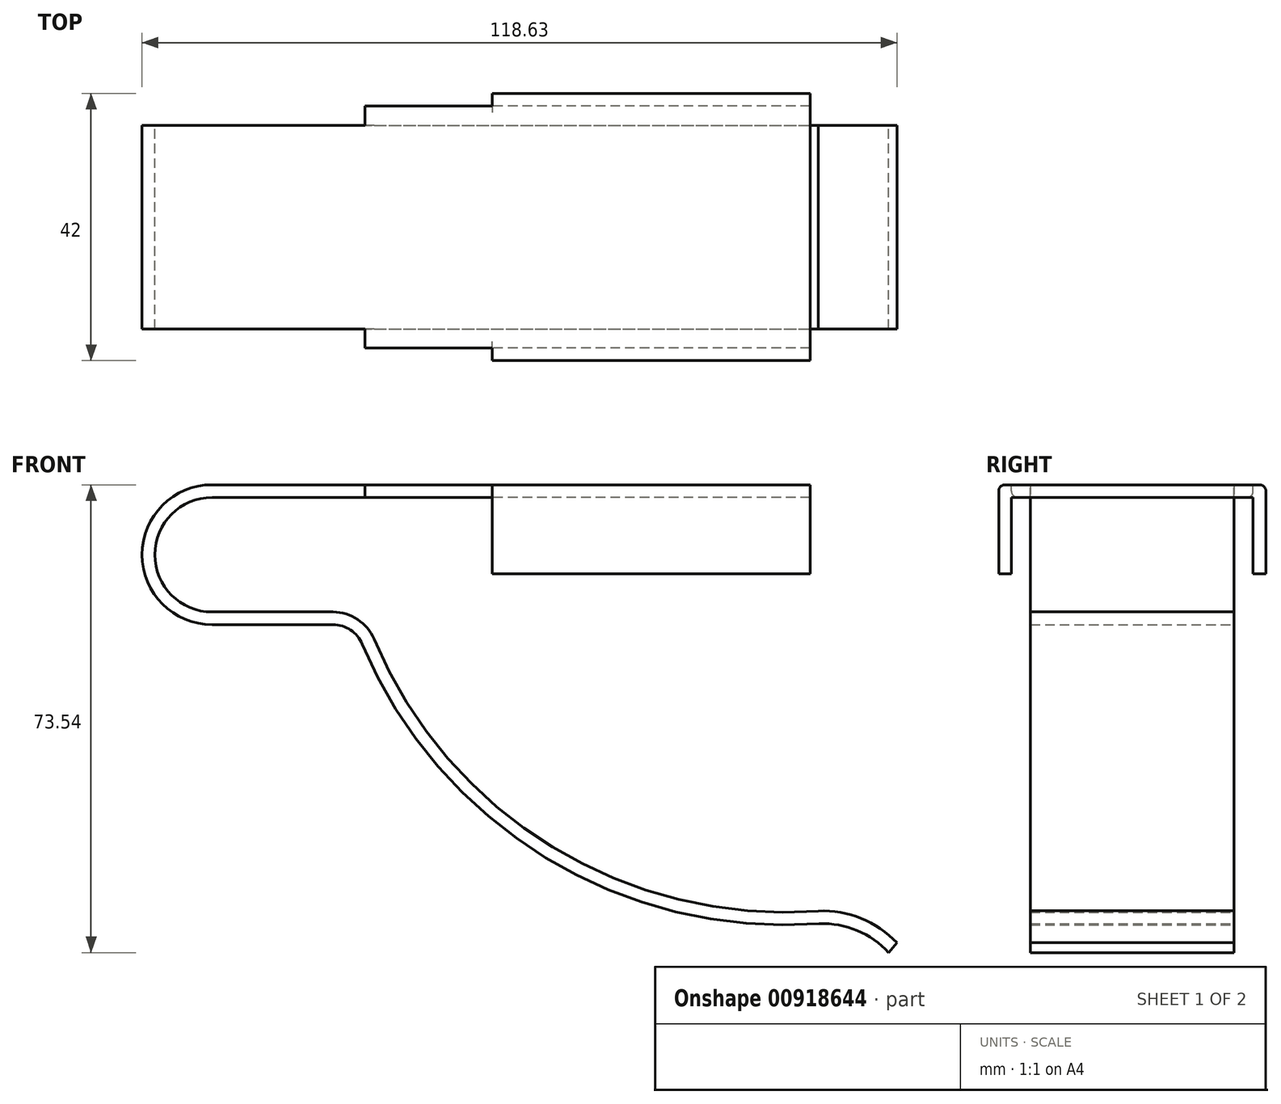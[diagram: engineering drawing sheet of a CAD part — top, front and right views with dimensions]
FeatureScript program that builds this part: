
annotation { "Feature Type Name" : "Feature", "Feature Type Description" : "" }
export const myFeature = defineFeature(function(context is Context, id is Id, definition is map)
    precondition{}
    {
        {
            var Q0;
            Q0=qCreatedBy(makeId("Front.planeOp"),FACE);
            var sketch = newSketch(context, id + "F0", { "sketchPlane" : qUnion([Q0])});
            skArc(sketch, "E0", {"start": v(0, 11) * mm, "mid": v(-11, 0) * mm, "end": v(0, -11) * mm});
            skLineSegment(sketch, "E1", {"start": v(0, 11) * mm, "end": v(94, 11) * mm});
            skLineSegment(sketch, "E2", {"start": v(0, -11) * mm, "end": v(19, -11) * mm});
            skArc(sketch, "E3", {"start": v(23.61, -14.06) * mm, "mid": v(52.42, -47.62) * mm, "end": v(95.41, -58) * mm});
            skArc(sketch, "E4", {"start": v(106.34, -62.54) * mm, "mid": v(101.38, -59.06) * mm, "end": v(95.41, -58) * mm});
            skPoint(sketch, "E5.visualSharp", {"position": v(22.4, -11) * mm});
            skArc(sketch, "E5.filletArc", {"start": v(23.61, -14.06) * mm, "mid": v(21.77, -11.84) * mm, "end": v(19, -11) * mm});
            skArc(sketch, "E6.0", {"start": v(107.63, -61) * mm, "mid": v(102, -57.16) * mm, "end": v(95.3, -56) * mm});
            skArc(sketch, "E6.1", {"start": v(25.45, -13.3) * mm, "mid": v(53.48, -45.92) * mm, "end": v(95.3, -56) * mm});
            skLineSegment(sketch, "E6.2", {"start": v(0, 9) * mm, "end": v(94, 9) * mm});
            skArc(sketch, "E6.3", {"start": v(0, 9) * mm, "mid": v(-9, 0) * mm, "end": v(0, -9) * mm});
            skLineSegment(sketch, "E6.4", {"start": v(0, -9) * mm, "end": v(19, -9) * mm});
            skArc(sketch, "E6.5", {"start": v(25.45, -13.3) * mm, "mid": v(22.88, -10.17) * mm, "end": v(19, -9) * mm});
            skLineSegment(sketch, "E7", {"start": v(94, 11) * mm, "end": v(94, 9) * mm});
            skLineSegment(sketch, "E8", {"start": v(106.34, -62.54) * mm, "end": v(107.63, -61) * mm});
            skSolve(sketch);
        }
        {
            var Q0;
            Q0=qSketchRegion(id+"F0",true);
            extrude(context, id + "F1", {"entities" : qUnion([Q0]), "depth" : 16 * mm, "offsetDistance" : 25 * mm});
        }
        {
            var Q0;
            Q0=makeQuery(id+"F1.opExtrude","SWEPT_FACE",FACE,{"disambiguationData":[OSD([sQuery(id+"F0.wireOp",EDGE,"E1")])]});
            var sketch = newSketch(context, id + "F2", { "sketchPlane" : qUnion([Q0])});
            skLineSegment(sketch, "E9.bottom", {"start": v(94, -16) * mm, "end": v(24, -16) * mm});
            skLineSegment(sketch, "E9.top", {"start": v(94, -19) * mm, "end": v(24, -19) * mm});
            skLineSegment(sketch, "E9.left", {"start": v(94, -16) * mm, "end": v(94, -19) * mm});
            skLineSegment(sketch, "E9.right", {"start": v(24, -16) * mm, "end": v(24, -19) * mm});
            skSolve(sketch);
        }
        {
            var Q0;
            Q0=makeQuery(id+"F2.imprint","IMPRINT",FACE,{"disambiguationData":[TD([[makeQuery(id+"F2.imprint","IMPRINT",EDGE,{"derivedFrom":sQuery(id+"F2.wireOp",EDGE,"E9.bottom")}),-1.0]])]});
            extrude(context, id + "F3", {"entities" : qUnion([Q0]), "operationType" : NewBodyOperationType.ADD, "oppositeDirection" : true, "depth" : 2 * mm, "offsetDistance" : 25 * mm});
        }
        {
            var Q0;
            Q0=makeQuery(id+"F3.opExtrude","SWEPT_FACE",FACE,{"disambiguationData":[OSD([sQuery(id+"F2.wireOp",EDGE,"E9.top")])]});
            var sketch = newSketch(context, id + "F4", { "sketchPlane" : qUnion([Q0])});
            skLineSegment(sketch, "E10.bottom", {"start": v(94, 11) * mm, "end": v(44, 11) * mm});
            skLineSegment(sketch, "E10.top", {"start": v(94, -3) * mm, "end": v(44, -3) * mm});
            skLineSegment(sketch, "E10.left", {"start": v(94, 11) * mm, "end": v(94, -3) * mm});
            skLineSegment(sketch, "E10.right", {"start": v(44, 11) * mm, "end": v(44, -3) * mm});
            skSolve(sketch);
        }
        {
            var Q0;
            Q0=qSketchRegion(id+"F4",true);
            extrude(context, id + "F5", {"entities" : qUnion([Q0]), "operationType" : NewBodyOperationType.ADD, "depth" : 2 * mm, "offsetDistance" : 25 * mm});
        }
        {
            var Q0;
            Q0=makeQuery(id+"F5.opExtrude","CAP_EDGE",EDGE,{"disambiguationData":[OSD([sQuery(id+"F4.wireOp",EDGE,"E10.bottom")])],"isStart":false});
            var Q1;
            {var subQ0=sQuery(id+"F2.wireOp",EDGE,"E9.top");Q1=makeQuery(id+"F5.boolean.opBoolean","SPLIT",EDGE,{"disambiguationData":[topologyDisambiguationEdgeConnected([makeQuery(id+"F5.opExtrude","CAP_FACE",FACE,{"disambiguationData":[OSD([sQuery(id+"F4.wireOp",EDGE,"E10.bottom"),sQuery(id+"F4.wireOp",EDGE,"E10.top"),sQuery(id+"F4.wireOp",EDGE,"E10.left"),sQuery(id+"F4.wireOp",EDGE,"E10.right")])],"isStart":true})])],"derivedFrom":makeQuery(id+"F3.opExtrude","CAP_EDGE",EDGE,{"disambiguationData":[OSD([subQ0])],"isStart":false})});}
            fillet(context, id + "F6", {"entities" : qUnion([Q0, Q1]), "radius" : 1 * mm, "tangentPropagation" : true, "allowEdgeOverflow" : false});
        }
        {
            var Q0;
            Q0=makeQuery(id+"F1.opExtrude","SWEPT_BODY",BODY,{"disambiguationData":[OSD([sQuery(id+"F0.wireOp",EDGE,"E0"),sQuery(id+"F0.wireOp",EDGE,"E1"),sQuery(id+"F0.wireOp",EDGE,"E2"),sQuery(id+"F0.wireOp",EDGE,"E3"),sQuery(id+"F0.wireOp",EDGE,"E4"),sQuery(id+"F0.wireOp",EDGE,"E5.filletArc"),sQuery(id+"F0.wireOp",EDGE,"E6.0"),sQuery(id+"F0.wireOp",EDGE,"E6.1"),sQuery(id+"F0.wireOp",EDGE,"E6.2"),sQuery(id+"F0.wireOp",EDGE,"E6.3"),sQuery(id+"F0.wireOp",EDGE,"E6.4"),sQuery(id+"F0.wireOp",EDGE,"E6.5"),sQuery(id+"F0.wireOp",EDGE,"E7"),sQuery(id+"F0.wireOp",EDGE,"E8")])]});
            var Q1;
            Q1=qCreatedBy(makeId("Front.planeOp"),FACE);
            mirror(context, id + "F7", {"operationType" : NewBodyOperationType.ADD, "entities" : qUnion([Q0]), "mirrorPlane" : qUnion([Q1])});
        }
    });
